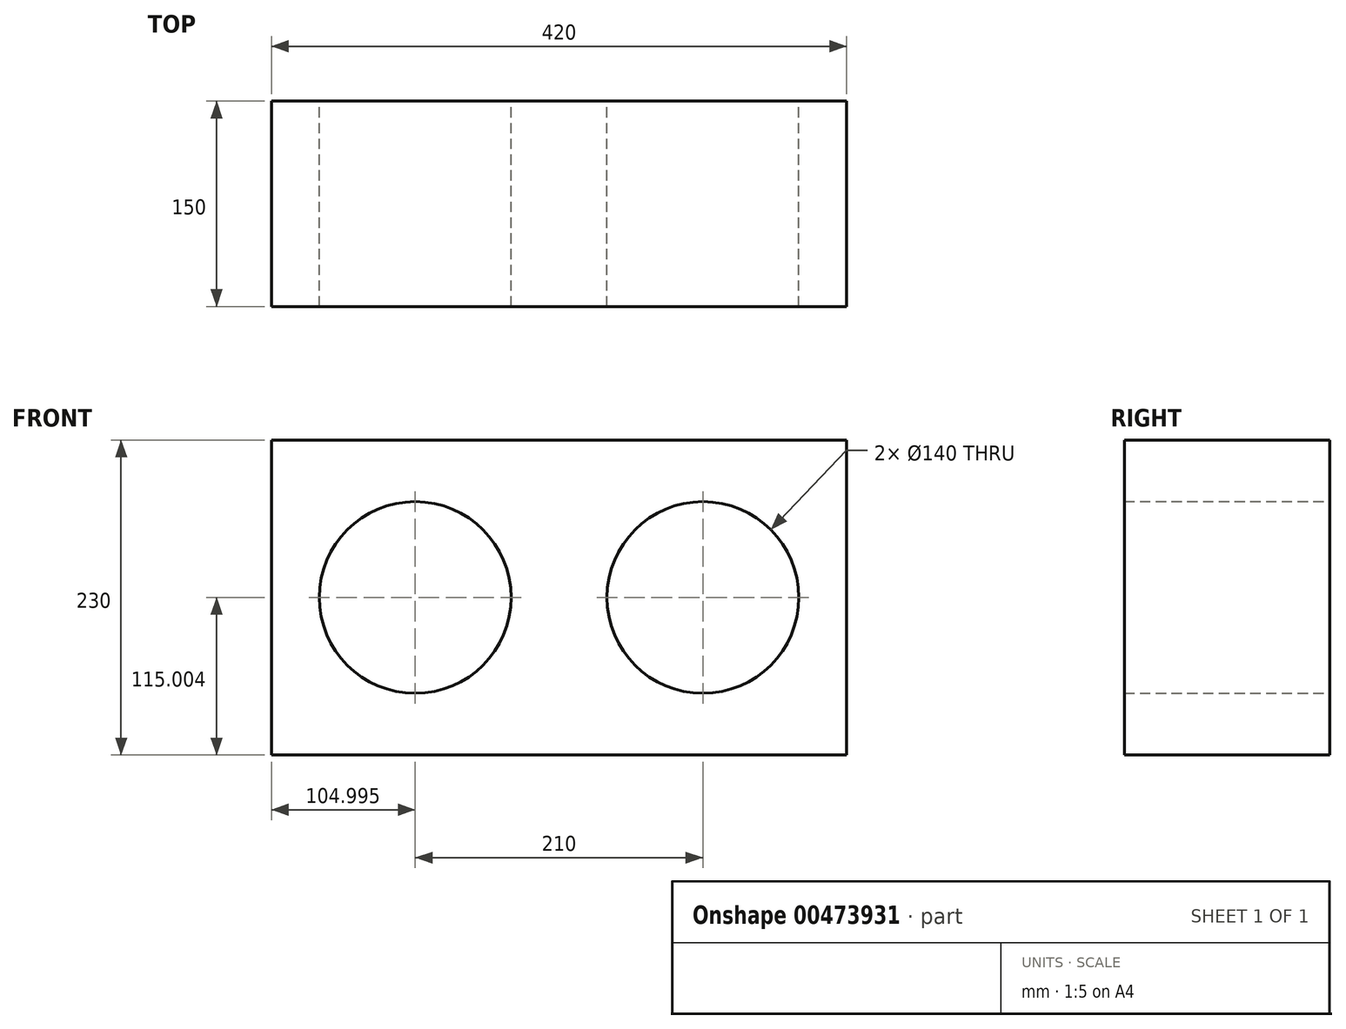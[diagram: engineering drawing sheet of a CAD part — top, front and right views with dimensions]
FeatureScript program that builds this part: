
annotation { "Feature Type Name" : "Feature", "Feature Type Description" : "" }
export const myFeature = defineFeature(function(context is Context, id is Id, definition is map)
    precondition{}
    {
        {
            var Q0;
            Q0=qCreatedBy(makeId("Front.planeOp"),FACE);
            var sketch = newSketch(context, id + "F0", { "sketchPlane" : qUnion([Q0])});
            skLineSegment(sketch, "E0.bottom", {"start": v(-50.73, 202.4) * mm, "end": v(369.27, 202.4) * mm});
            skLineSegment(sketch, "E0.top", {"start": v(-50.73, -27.6) * mm, "end": v(369.27, -27.6) * mm});
            skLineSegment(sketch, "E0.left", {"start": v(-50.73, 202.4) * mm, "end": v(-50.73, -27.6) * mm});
            skLineSegment(sketch, "E0.right", {"start": v(369.27, 202.4) * mm, "end": v(369.27, -27.6) * mm});
            skCircle(sketch, "E1", {"center": v(54.27, 87.4) * mm, "radius": 70 * mm});
            skCircle(sketch, "E2", {"center": v(264.27, 87.4) * mm, "radius": 70 * mm});
            skSolve(sketch);
        }
        {
            var Q0;
            Q0=makeQuery(id+"F0.imprint","IMPRINT",FACE,{"disambiguationData":[TD([[makeQuery(id+"F0.imprint","IMPRINT",EDGE,{"derivedFrom":sQuery(id+"F0.wireOp",EDGE,"E0.bottom")}),-1.0]])]});
            extrude(context, id + "F1", {"entities" : qUnion([Q0]), "depth" : 150 * mm});
        }
    });
